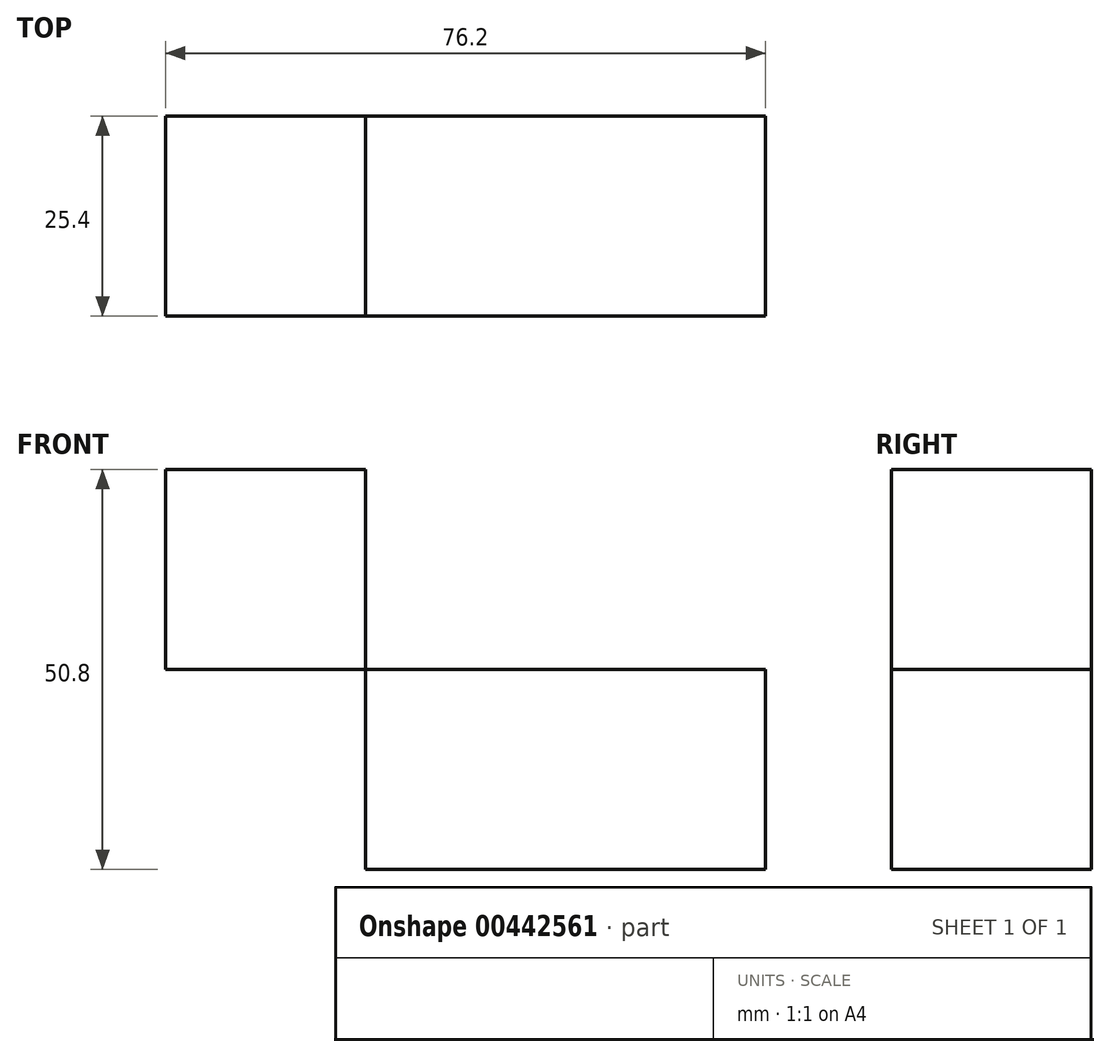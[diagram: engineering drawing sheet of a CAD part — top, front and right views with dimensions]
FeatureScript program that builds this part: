
annotation { "Feature Type Name" : "Feature", "Feature Type Description" : "" }
export const myFeature = defineFeature(function(context is Context, id is Id, definition is map)
    precondition{}
    {
        {
            var Q0;
            Q0=qCreatedBy(makeId("Front.planeOp"),FACE);
            var sketch = newSketch(context, id + "F0", { "sketchPlane" : qUnion([Q0])});
            skLineSegment(sketch, "E0.bottom", {"start": v(0, 0) * mm, "end": v(25.4, 0) * mm});
            skLineSegment(sketch, "E0.top", {"start": v(0, 25.4) * mm, "end": v(25.4, 25.4) * mm});
            skLineSegment(sketch, "E0.left", {"start": v(0, 0) * mm, "end": v(0, 25.4) * mm});
            skLineSegment(sketch, "E0.right", {"start": v(25.4, 0) * mm, "end": v(25.4, 25.4) * mm});
            skLineSegment(sketch, "E1.bottom", {"start": v(0, 25.4) * mm, "end": v(-25.4, 25.4) * mm});
            skLineSegment(sketch, "E1.top", {"start": v(0, 0) * mm, "end": v(-25.4, 0) * mm});
            skLineSegment(sketch, "E1.left", {"start": v(0, 25.4) * mm, "end": v(0, 0) * mm});
            skLineSegment(sketch, "E1.right", {"start": v(-25.4, 25.4) * mm, "end": v(-25.4, 0) * mm});
            skLineSegment(sketch, "E2.bottom", {"start": v(-25.4, 25.4) * mm, "end": v(0, 25.4) * mm});
            skLineSegment(sketch, "E2.top", {"start": v(-25.4, 50.8) * mm, "end": v(0, 50.8) * mm});
            skLineSegment(sketch, "E2.left", {"start": v(-25.4, 25.4) * mm, "end": v(-25.4, 50.8) * mm});
            skLineSegment(sketch, "E2.right", {"start": v(0, 25.4) * mm, "end": v(0, 50.8) * mm});
            skLineSegment(sketch, "E3.bottom", {"start": v(-25.4, 50.8) * mm, "end": v(-50.8, 50.8) * mm});
            skLineSegment(sketch, "E3.top", {"start": v(-25.4, 25.4) * mm, "end": v(-50.8, 25.4) * mm});
            skLineSegment(sketch, "E3.left", {"start": v(-25.4, 50.8) * mm, "end": v(-25.4, 25.4) * mm});
            skLineSegment(sketch, "E3.right", {"start": v(-50.8, 50.8) * mm, "end": v(-50.8, 25.4) * mm});
            skLineSegment(sketch, "E4.bottom", {"start": v(-50.8, 50.8) * mm, "end": v(-25.4, 50.8) * mm});
            skLineSegment(sketch, "E4.top", {"start": v(-50.8, 75.4) * mm, "end": v(-25.4, 75.4) * mm});
            skLineSegment(sketch, "E4.left", {"start": v(-50.8, 50.8) * mm, "end": v(-50.8, 75.4) * mm});
            skLineSegment(sketch, "E4.right", {"start": v(-25.4, 50.8) * mm, "end": v(-25.4, 75.4) * mm});
            skSolve(sketch);
        }
        {
            var Q0;
            Q0=makeQuery(id+"F0.imprint","IMPRINT",FACE,{"disambiguationData":[TD([[makeQuery(id+"F0.imprint","IMPRINT",EDGE,{"derivedFrom":sQuery(id+"F0.wireOp",EDGE,"E4.bottom")}),1.0]])]});
            var Q1;
            Q1=makeQuery(id+"F0.imprint","IMPRINT",FACE,{"disambiguationData":[TD([[makeQuery(id+"F0.imprint","IMPRINT",EDGE,{"derivedFrom":sQuery(id+"F0.wireOp",EDGE,"E3.top")}),-1.0]])]});
            var Q2;
            Q2=makeQuery(id+"F0.imprint","IMPRINT",FACE,{"disambiguationData":[TD([[makeQuery(id+"F0.imprint","IMPRINT",EDGE,{"derivedFrom":sQuery(id+"F0.wireOp",EDGE,"E2.bottom")}),1.0]])]});
            var Q3;
            Q3=makeQuery(id+"F0.imprint","IMPRINT",FACE,{"disambiguationData":[TD([[makeQuery(id+"F0.imprint","IMPRINT",EDGE,{"derivedFrom":sQuery(id+"F0.wireOp",EDGE,"E1.top")}),-1.0]])]});
            var Q4;
            Q4=makeQuery(id+"F0.imprint","IMPRINT",FACE,{"disambiguationData":[TD([[makeQuery(id+"F0.imprint","IMPRINT",EDGE,{"derivedFrom":sQuery(id+"F0.wireOp",EDGE,"E0.bottom")}),1.0]])]});
            extrude(context, id + "F1", {"entities" : qUnion([Q0, Q1, Q2, Q3, Q4]), "depth" : 25.4 * mm});
        }
    });
